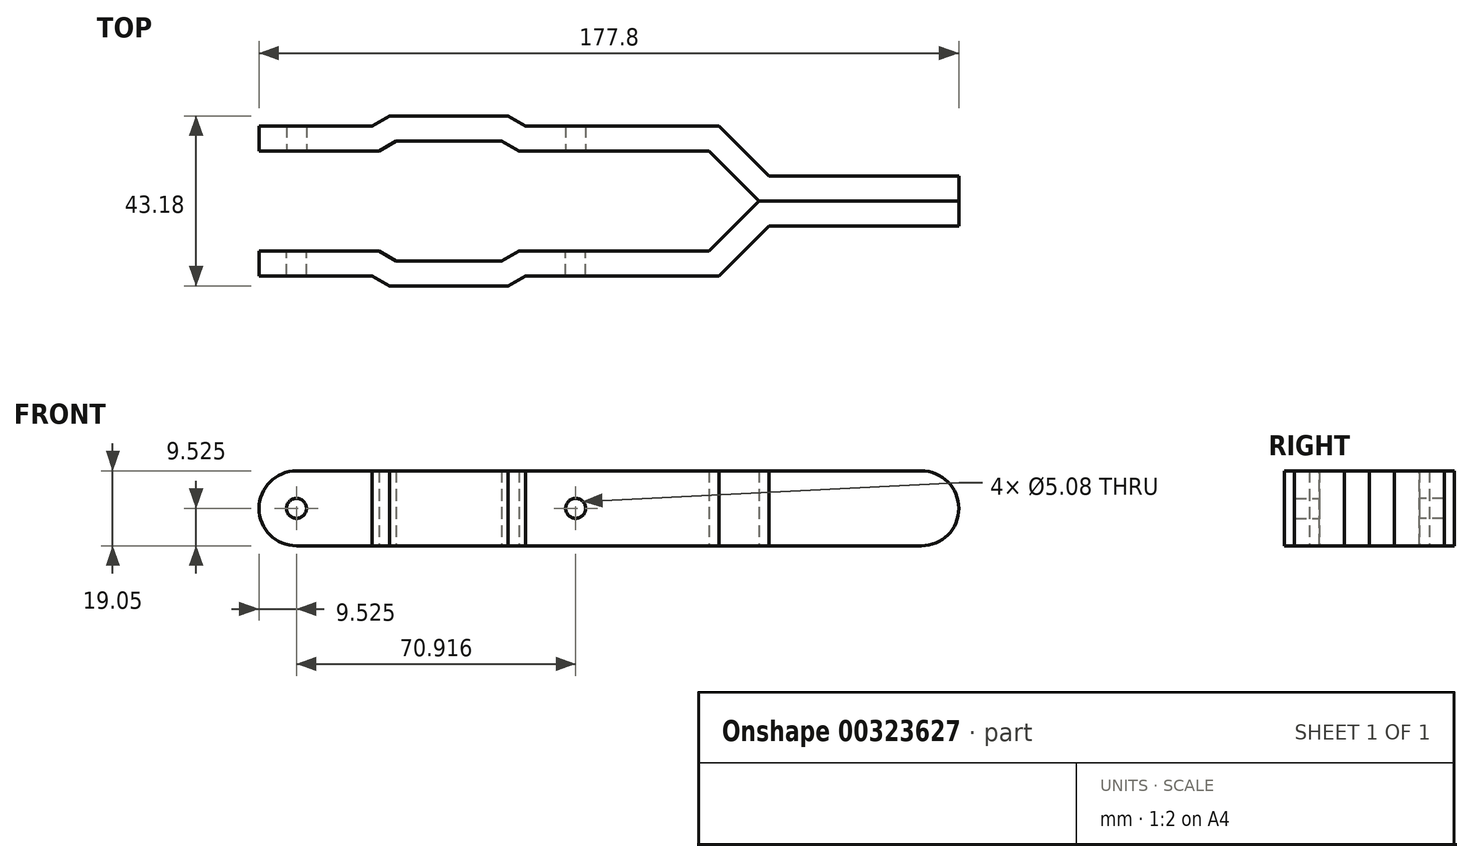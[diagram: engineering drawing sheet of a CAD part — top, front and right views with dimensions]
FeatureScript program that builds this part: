
annotation { "Feature Type Name" : "Feature", "Feature Type Description" : "" }
export const myFeature = defineFeature(function(context is Context, id is Id, definition is map)
    precondition{}
    {
        {
            var Q0;
            Q0=qCreatedBy(makeId("Top.planeOp"),FACE);
            var sketch = newSketch(context, id + "F0", { "sketchPlane" : qUnion([Q0])});
            skLineSegment(sketch, "E0", {"start": v(-2.54, -12.7) * mm, "end": v(27.94, -12.7) * mm});
            skLineSegment(sketch, "E1", {"start": v(32.34, -15.24) * mm, "end": v(27.94, -12.7) * mm});
            skLineSegment(sketch, "E2", {"start": v(32.34, -15.24) * mm, "end": v(59.1, -15.24) * mm});
            skLineSegment(sketch, "E3", {"start": v(63.5, -12.7) * mm, "end": v(111.76, -12.7) * mm});
            skLineSegment(sketch, "E4", {"start": v(124.46, 0) * mm, "end": v(111.76, -12.7) * mm});
            skLineSegment(sketch, "E5", {"start": v(124.46, 0) * mm, "end": v(175.26, 0) * mm});
            skLineSegment(sketch, "E6", {"start": v(59.1, -15.24) * mm, "end": v(63.5, -12.7) * mm});
            skLineSegment(sketch, "E7.0", {"start": v(-2.54, -19.05) * mm, "end": v(26.24, -19.05) * mm});
            skLineSegment(sketch, "E7.1", {"start": v(30.64, -21.6) * mm, "end": v(26.24, -19.05) * mm});
            skLineSegment(sketch, "E7.2", {"start": v(30.64, -21.59) * mm, "end": v(60.8, -21.59) * mm});
            skLineSegment(sketch, "E7.3", {"start": v(127.1, -6.35) * mm, "end": v(175.26, -6.35) * mm});
            skLineSegment(sketch, "E7.4", {"start": v(127.1, -6.35) * mm, "end": v(114.4, -19.05) * mm});
            skLineSegment(sketch, "E7.5", {"start": v(65.2, -19.05) * mm, "end": v(114.4, -19.05) * mm});
            skLineSegment(sketch, "E7.6", {"start": v(60.8, -21.6) * mm, "end": v(65.2, -19.05) * mm});
            skLineSegment(sketch, "E8", {"start": v(-2.54, -12.7) * mm, "end": v(-2.54, -19.05) * mm});
            skLineSegment(sketch, "E9", {"start": v(175.26, 0) * mm, "end": v(175.26, -6.35) * mm});
            skSolve(sketch);
        }
        {
            var Q0;
            Q0 = qSketchRegion(id + "F0", true);
            extrude(context, id + "F1", {"entities" : qUnion([Q0]), "depth" : 19.05 * mm});
        }
        {
            var Q0;
            Q0=makeQuery(id+"F1.opExtrude","CAP_EDGE",EDGE,{"disambiguationData":[OSD([sQuery(id+"F0.wireOp",EDGE,"E8")])],"isStart":false});
            var Q1;
            Q1=makeQuery(id+"F1.opExtrude","CAP_EDGE",EDGE,{"disambiguationData":[OSD([sQuery(id+"F0.wireOp",EDGE,"E8")])],"isStart":true});
            var Q2;
            Q2=makeQuery(id+"F1.opExtrude","CAP_EDGE",EDGE,{"disambiguationData":[OSD([sQuery(id+"F0.wireOp",EDGE,"E9")])],"isStart":false});
            var Q3;
            Q3=makeQuery(id+"F1.opExtrude","CAP_EDGE",EDGE,{"disambiguationData":[OSD([sQuery(id+"F0.wireOp",EDGE,"E9")])],"isStart":true});
            fillet(context, id + "F2", {"entities" : qUnion([Q0, Q1, Q2, Q3]), "radius" : 9.52 * mm, "tangentPropagation" : true, "allowEdgeOverflow" : false});
        }
        {
            var Q0;
            Q0=qCreatedBy(makeId("Front.planeOp"),FACE);
            var sketch = newSketch(context, id + "F3", { "sketchPlane" : qUnion([Q0])});
            skPoint(sketch, "E10", {"position": v(6.98, 9.52) * mm});
            skPoint(sketch, "E11", {"position": v(77.9, 9.52) * mm});
            skCircle(sketch, "E12", {"center": v(6.98, 9.52) * mm, "radius": 2.54 * mm});
            skCircle(sketch, "E13", {"center": v(77.9, 9.52) * mm, "radius": 2.54 * mm});
            skSolve(sketch);
        }
        {
            var Q0;
            Q0 = qSketchRegion(id + "F3", true);
            extrude(context, id + "F4", {"entities" : qUnion([Q0]), "operationType" : NewBodyOperationType.REMOVE, "depth" : 25.4 * mm});
        }
        {
            var Q0;
            Q0=makeQuery(id+"F1.opExtrude","SWEPT_BODY",BODY,{"disambiguationData":[OSD([sQuery(id+"F0.wireOp",EDGE,"E0"),sQuery(id+"F0.wireOp",EDGE,"E1"),sQuery(id+"F0.wireOp",EDGE,"E2"),sQuery(id+"F0.wireOp",EDGE,"E3"),sQuery(id+"F0.wireOp",EDGE,"E4"),sQuery(id+"F0.wireOp",EDGE,"E5"),sQuery(id+"F0.wireOp",EDGE,"E6"),sQuery(id+"F0.wireOp",EDGE,"E7.0"),sQuery(id+"F0.wireOp",EDGE,"E7.1"),sQuery(id+"F0.wireOp",EDGE,"E7.2"),sQuery(id+"F0.wireOp",EDGE,"E7.3"),sQuery(id+"F0.wireOp",EDGE,"E7.4"),sQuery(id+"F0.wireOp",EDGE,"E7.5"),sQuery(id+"F0.wireOp",EDGE,"E7.6"),sQuery(id+"F0.wireOp",EDGE,"E8"),sQuery(id+"F0.wireOp",EDGE,"E9")])]});
            var Q1;
            Q1=qCreatedBy(makeId("Front.planeOp"),FACE);
            mirror(context, id + "F5", {"entities" : qUnion([Q0]), "mirrorPlane" : qUnion([Q1])});
        }
    });
